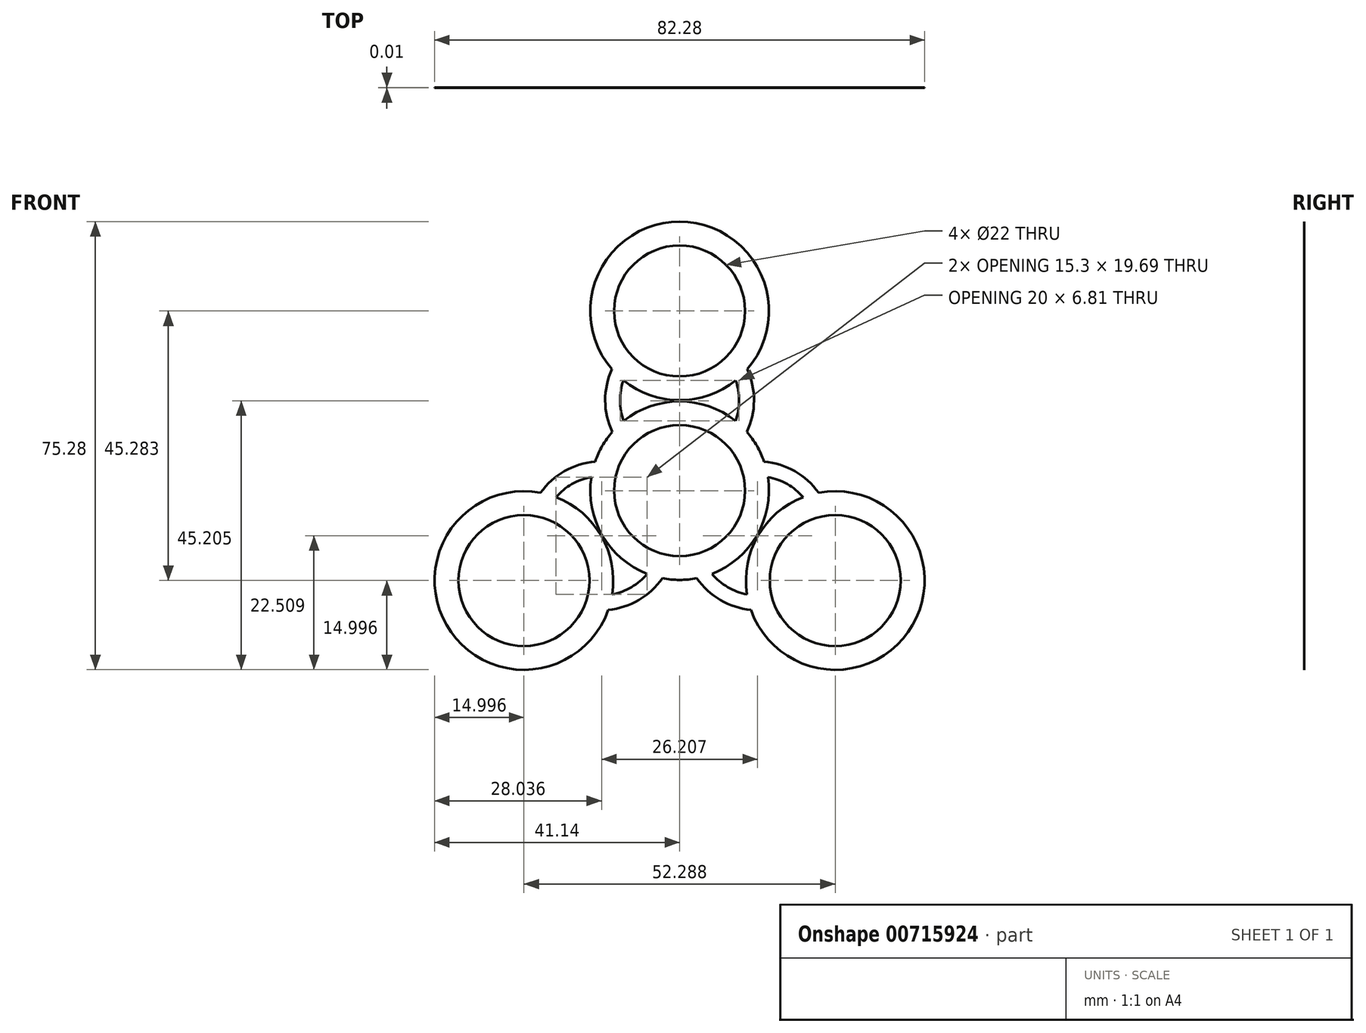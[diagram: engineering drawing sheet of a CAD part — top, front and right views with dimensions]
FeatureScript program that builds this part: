
annotation { "Feature Type Name" : "Feature", "Feature Type Description" : "" }
export const myFeature = defineFeature(function(context is Context, id is Id, definition is map)
    precondition{}
    {
        {
            var Q0;
            Q0=qCreatedBy(makeId("Front.planeOp"),FACE);
            var sketch = newSketch(context, id + "F0", { "sketchPlane" : qUnion([Q0])});
            skCircle(sketch, "E0", {"center": v(0, 0) * mm, "radius": 50.8 * mm, "construction": true});
            skCircle(sketch, "E1", {"center": v(0, 0) * mm, "radius": 11 * mm});
            skCircle(sketch, "E2", {"center": v(0, 0) * mm, "radius": 15 * mm});
            skCircle(sketch, "E3", {"center": v(0, 30.19) * mm, "radius": 15 * mm});
            skCircle(sketch, "E4", {"center": v(0, 30.19) * mm, "radius": 11 * mm});
            skCircle(sketch, "E5.1.0", {"center": v(-26.14, -15.1) * mm, "radius": 11 * mm});
            skCircle(sketch, "E5.2.0", {"center": v(26.14, -15.1) * mm, "radius": 11 * mm});
            skCircle(sketch, "E6.1.0", {"center": v(-26.14, -15.1) * mm, "radius": 15 * mm});
            skCircle(sketch, "E6.2.0", {"center": v(26.14, -15.1) * mm, "radius": 15 * mm});
            skArc(sketch, "E7", {"start": v(-11.36, 20.4) * mm, "mid": v(-12.5, 15.12) * mm, "end": v(-11.3, 9.86) * mm});
            skArc(sketch, "E8", {"start": v(-9.43, 18.52) * mm, "mid": v(-10, 15.11) * mm, "end": v(-9.38, 11.7) * mm});
            skArc(sketch, "E9.1.0", {"start": v(-14.83, 2.26) * mm, "mid": v(-18.09, 1.1) * mm, "end": v(-20.75, -1.1) * mm});
            skArc(sketch, "E9.1.1", {"start": v(-14.19, 4.86) * mm, "mid": v(-19.34, 3.26) * mm, "end": v(-23.35, -0.36) * mm});
            skArc(sketch, "E9.2.0", {"start": v(5.45, -13.97) * mm, "mid": v(8.09, -16.22) * mm, "end": v(11.33, -17.43) * mm});
            skArc(sketch, "E9.2.1", {"start": v(2.88, -14.72) * mm, "mid": v(6.85, -18.39) * mm, "end": v(11.98, -20.04) * mm});
            skArc(sketch, "E10.trimOffspring", {"start": v(9.38, 11.7) * mm, "mid": v(10, 15.11) * mm, "end": v(9.43, 18.52) * mm});
            skArc(sketch, "E11.trimOffspring", {"start": v(11.3, 9.86) * mm, "mid": v(12.5, 15.12) * mm, "end": v(11.36, 20.4) * mm});
            skArc(sketch, "E12.trimOffspring", {"start": v(20.75, -1.1) * mm, "mid": v(18.09, 1.1) * mm, "end": v(14.83, 2.26) * mm});
            skArc(sketch, "E13.trimOffspring", {"start": v(23.35, -0.36) * mm, "mid": v(19.34, 3.26) * mm, "end": v(14.19, 4.86) * mm});
            skArc(sketch, "E14.trimOffspring", {"start": v(-11.33, -17.43) * mm, "mid": v(-8.09, -16.22) * mm, "end": v(-5.45, -13.97) * mm});
            skArc(sketch, "E15.trimOffspring", {"start": v(-11.98, -20.04) * mm, "mid": v(-6.85, -18.39) * mm, "end": v(-2.88, -14.72) * mm});
            skSolve(sketch);
        }
        {
            var Q0;
            Q0 = qSketchRegion(id + "F0", true);
            extrude(context, id + "F1", {"entities" : qUnion([Q0]), "oppositeDirection" : true, "depth" : 1 / 101.6 * mm, "offsetDistance" : 25 * mm});
        }
    });
